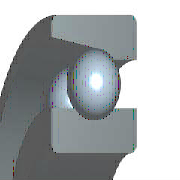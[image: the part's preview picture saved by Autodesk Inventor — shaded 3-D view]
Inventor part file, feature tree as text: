
AUTODESK INVENTOR PART (.ipt)
format: ipt  version: 2025.2 (Build 292293000, 293)  size: 270,848 bytes
history: native  units: mm (DEFAULTED — no unit token found)
features: other x2, pattern_circular x1
ambient origin geometry x8: Origin, YZ Plane, XZ Plane, XY Plane, X Axis, Y Axis, Z Axis, Center Point
bodies: Solid1 (feature_tree)
feature tree (3):
  other  "Körper"
  other  "Kugel"
  pattern_circular  "Kugeln"  [2 undecoded]
note: 2 required parameter values undecoded (feature->parameter linkage not recoverable at this tier; creation-order binding heuristic only, values carry confidence <= 0.55)
